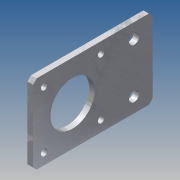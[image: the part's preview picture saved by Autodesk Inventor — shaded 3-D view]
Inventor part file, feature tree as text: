
AUTODESK INVENTOR PART (.ipt)
format: ipt  version: 2015 SP1 (Build 190203100, 203)  size: 126,464 bytes
history: native  units: mm
features: extrude x1, sketch x1
ambient origin geometry x8: Origin, YZ Plane, XZ Plane, XY Plane, X Axis, Y Axis, Z Axis, Center Point
bodies: Body1 (feature_tree)
feature tree (2):
  extrude  "Extrusion5"  Depth=43.0mm
  sketch  "Skizze1"  dims[d0=65.0mm d1=43.0mm d2=5.5mm d3=10.0mm d4=8.0mm d14=2.0mm d15=2.0mm d16=2.0mm d17=2.0mm d18=2.0mm d19=2.0mm d20=2.0mm d21=2.0mm d35=24.0mm d43=3.5mm d44=15.5mm d46=15.5mm d47=21.5mm d48=3.5mm d49=15.5mm d50=15.5mm d51=3.0mm d52=0.0mm]
